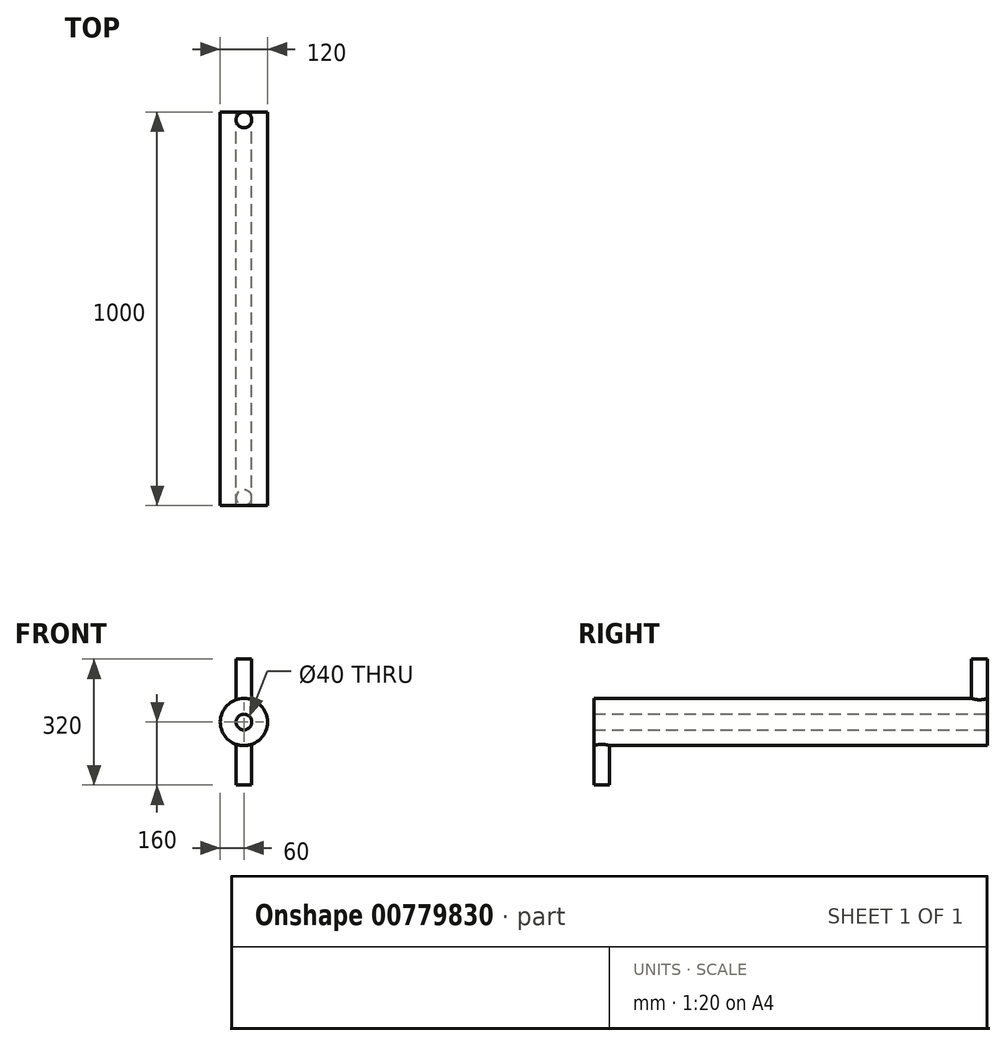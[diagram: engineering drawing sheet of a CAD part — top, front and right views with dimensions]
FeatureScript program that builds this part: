
annotation { "Feature Type Name" : "Feature", "Feature Type Description" : "" }
export const myFeature = defineFeature(function(context is Context, id is Id, definition is map)
    precondition{}
    {
        {
            var Q0;
            Q0=qCreatedBy(makeId("Front.planeOp"),FACE);
            var sketch = newSketch(context, id + "F0", { "sketchPlane" : qUnion([Q0])});
            skCircle(sketch, "E0", {"center": v(0, 0) * mm, "radius": 20 * mm});
            skCircle(sketch, "E1", {"center": v(0, 0) * mm, "radius": 60 * mm});
            skSolve(sketch);
        }
        {
            var Q0;
            Q0=makeQuery(id+"F0.imprint","IMPRINT",FACE,{"disambiguationData":[TD([[makeQuery(id+"F0.imprint","IMPRINT",EDGE,{"derivedFrom":sQuery(id+"F0.wireOp",EDGE,"E0")}),-1.0]])]});
            extrude(context, id + "F1", {"entities" : qUnion([Q0]), "depth" : 1000 * mm, "offsetDistance" : 25 * mm});
        }
        {
            var Q0;
            Q0=qCreatedBy(makeId("Top.planeOp"),FACE);
            var Q1;
            Q1 = qBodyType(qCreatedBy(id + "FehisXvuLEzeXCV_1" ,EDGE), BodyType.WIRE);
            cPlane(context, id + "F2", {"entities" : qUnion([Q0, Q1]), "cplaneType" : CPlaneType.OFFSET, "offset" : 60 * mm, "width" : 150 * mm, "height" : 150 * mm});
        }
        {
            var Q0;
            Q0=qCreatedBy(id+"F2.planeOp",FACE);
            var sketch = newSketch(context, id + "F3", { "sketchPlane" : qUnion([Q0])});
            skCircle(sketch, "E2", {"center": v(0, -20) * mm, "radius": 20 * mm});
            skSolve(sketch);
        }
        {
            var Q0;
            Q0 = qSketchRegion(id + "F3", true);
            extrude(context, id + "F4", {"entities" : qUnion([Q0]), "operationType" : NewBodyOperationType.ADD, "depth" : 100 * mm, "offsetDistance" : 25 * mm, "hasSecondDirection" : true, "secondDirectionOppositeDirection" : true, "secondDirectionDepth" : 7 * mm});
        }
        {
            var Q0;
            Q0=qCreatedBy(makeId("Top.planeOp"),FACE);
            cPlane(context, id + "F5", {"entities" : qUnion([Q0]), "cplaneType" : CPlaneType.OFFSET, "offset" : 60 * mm, "oppositeDirection" : true, "width" : 150 * mm, "height" : 150 * mm});
        }
        {
            var Q0;
            Q0=qCreatedBy(id+"F5.planeOp",FACE);
            var sketch = newSketch(context, id + "F6", { "sketchPlane" : qUnion([Q0])});
            skCircle(sketch, "E3", {"center": v(0, -980) * mm, "radius": 20 * mm});
            skSolve(sketch);
        }
        {
            var Q0;
            Q0 = qSketchRegion(id + "F6", true);
            var Q1;
            Q1=sQuery(id+"F6.wireOp",EDGE,"E3");
            extrude(context, id + "F7", {"entities" : qUnion([Q0]), "operationType" : NewBodyOperationType.ADD, "surfaceEntities" : qUnion([Q1]), "oppositeDirection" : true, "depth" : 100 * mm, "offsetDistance" : 25 * mm, "hasSecondDirection" : true, "secondDirectionOppositeDirection" : false, "secondDirectionDepth" : 7 * mm});
        }
    });
